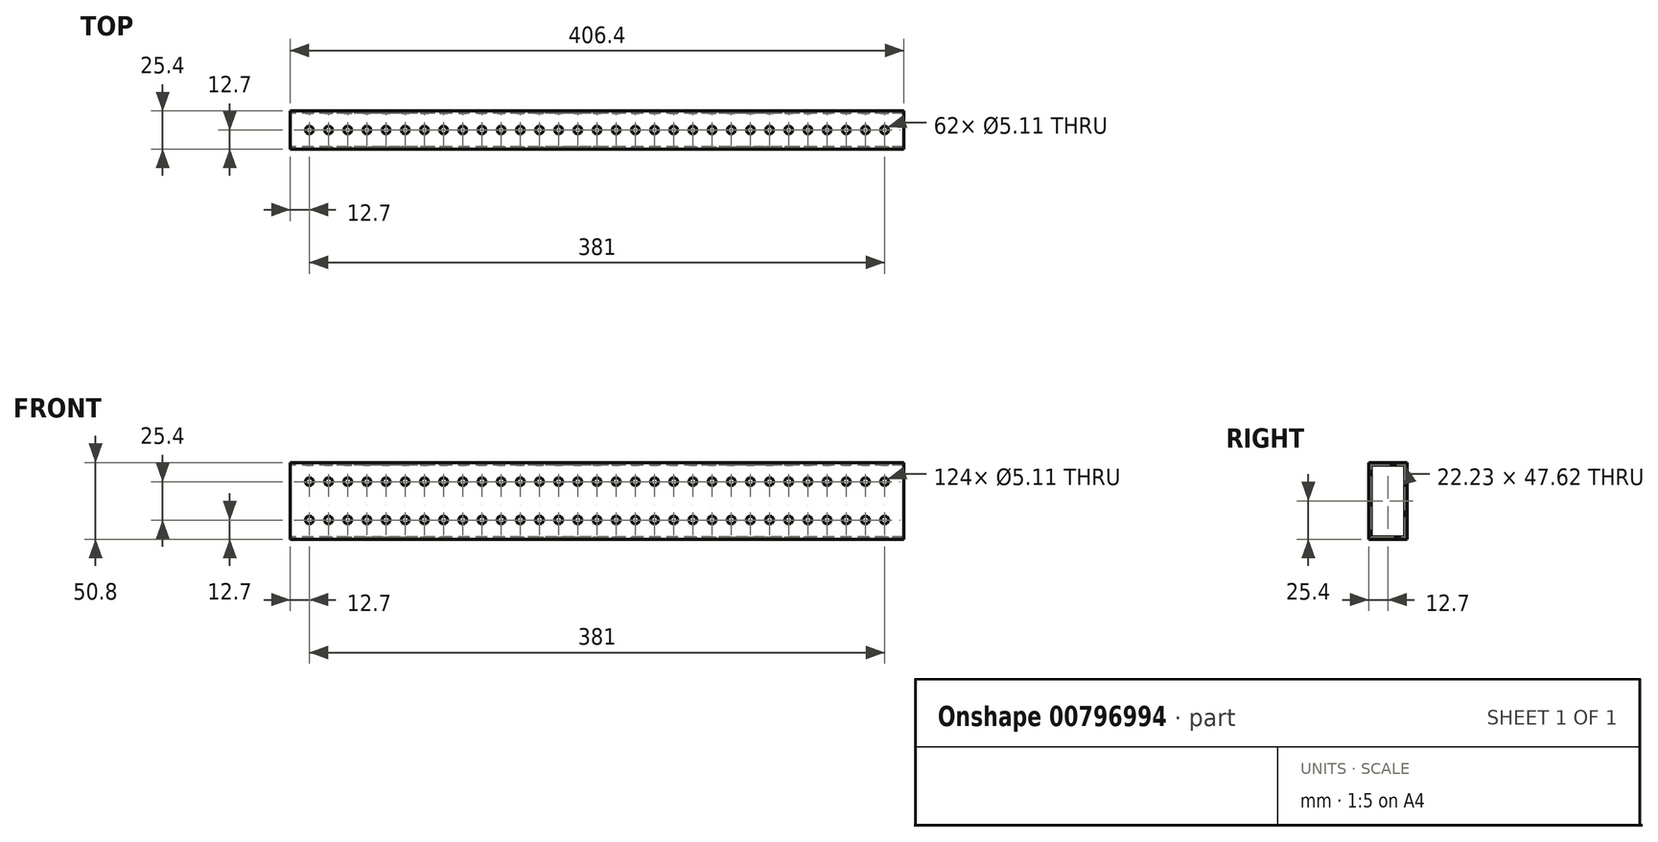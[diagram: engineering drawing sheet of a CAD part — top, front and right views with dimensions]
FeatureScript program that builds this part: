
annotation { "Feature Type Name" : "Feature", "Feature Type Description" : "" }
export const myFeature = defineFeature(function(context is Context, id is Id, definition is map)
    precondition{}
    {
        {
            var Q0;
            Q0=qCreatedBy(makeId("Right.planeOp"),FACE);
            var sketch = newSketch(context, id + "F0", { "sketchPlane" : qUnion([Q0])});
            skLineSegment(sketch, "E0.bottom", {"start": v(12.7, 25.4) * mm, "end": v(-12.7, 25.4) * mm});
            skLineSegment(sketch, "E0.top", {"start": v(12.7, -25.4) * mm, "end": v(-12.7, -25.4) * mm});
            skLineSegment(sketch, "E0.left", {"start": v(12.7, 25.4) * mm, "end": v(12.7, -25.4) * mm});
            skLineSegment(sketch, "E0.right", {"start": v(-12.7, 25.4) * mm, "end": v(-12.7, -25.4) * mm});
            skPoint(sketch, "E0.middle", {"position": v(0, 0) * mm});
            skLineSegment(sketch, "E1.0", {"start": v(-11.11, 23.81) * mm, "end": v(-11.11, -23.81) * mm});
            skLineSegment(sketch, "E1.1", {"start": v(11.11, 23.81) * mm, "end": v(-11.11, 23.81) * mm});
            skLineSegment(sketch, "E1.2", {"start": v(11.11, 23.81) * mm, "end": v(11.11, -23.81) * mm});
            skLineSegment(sketch, "E1.3", {"start": v(11.11, -23.81) * mm, "end": v(-11.11, -23.81) * mm});
            skSolve(sketch);
        }
        {
            var Q0;
            Q0 = qSketchRegion(id + "F0", true);
            extrude(context, id + "F1", {"entities" : qUnion([Q0]), "depth" : 406.4 * mm, "offsetDistance" : 25.4 * mm});
        }
        {
            var Q0;
            Q0=makeQuery(id+"F1.opExtrude","SWEPT_FACE",FACE,{"disambiguationData":[OSD([sQuery(id+"F0.wireOp",EDGE,"E0.bottom")])]});
            var sketch = newSketch(context, id + "F2", { "sketchPlane" : qUnion([Q0])});
            skCircle(sketch, "E2", {"center": v(12.7, 0) * mm, "radius": 2.55 * mm});
            skCircle(sketch, "E3.1.0.0", {"center": v(25.4, 0) * mm, "radius": 2.55 * mm});
            skCircle(sketch, "E3.2.0.0", {"center": v(38.1, 0) * mm, "radius": 2.55 * mm});
            skLineSegment(sketch, "E3.direction1", {"start": v(12.7, 0) * mm, "end": v(25.4, 0) * mm, "construction": true});
            skCircle(sketch, "E4.0.3.0", {"center": v(50.8, 0) * mm, "radius": 2.55 * mm});
            skCircle(sketch, "E4.0.4.0", {"center": v(63.5, 0) * mm, "radius": 2.55 * mm});
            skCircle(sketch, "E4.0.5.0", {"center": v(76.2, 0) * mm, "radius": 2.55 * mm});
            skCircle(sketch, "E4.0.6.0", {"center": v(88.9, 0) * mm, "radius": 2.55 * mm});
            skCircle(sketch, "E4.0.7.0", {"center": v(101.6, 0) * mm, "radius": 2.55 * mm});
            skCircle(sketch, "E4.0.8.0", {"center": v(114.3, 0) * mm, "radius": 2.55 * mm});
            skCircle(sketch, "E4.0.9.0", {"center": v(127, 0) * mm, "radius": 2.55 * mm});
            skCircle(sketch, "E4.0.10.0", {"center": v(139.7, 0) * mm, "radius": 2.55 * mm});
            skCircle(sketch, "E4.0.11.0", {"center": v(152.4, 0) * mm, "radius": 2.55 * mm});
            skCircle(sketch, "E4.0.12.0", {"center": v(165.1, 0) * mm, "radius": 2.55 * mm});
            skCircle(sketch, "E4.0.13.0", {"center": v(177.8, 0) * mm, "radius": 2.55 * mm});
            skCircle(sketch, "E4.0.14.0", {"center": v(190.5, 0) * mm, "radius": 2.55 * mm});
            skCircle(sketch, "E4.0.15.0", {"center": v(203.2, 0) * mm, "radius": 2.55 * mm});
            skCircle(sketch, "E4.0.16.0", {"center": v(215.9, 0) * mm, "radius": 2.55 * mm});
            skCircle(sketch, "E4.0.17.0", {"center": v(228.6, 0) * mm, "radius": 2.55 * mm});
            skCircle(sketch, "E4.0.18.0", {"center": v(241.3, 0) * mm, "radius": 2.55 * mm});
            skCircle(sketch, "E4.0.19.0", {"center": v(254, 0) * mm, "radius": 2.55 * mm});
            skCircle(sketch, "E4.0.20.0", {"center": v(266.7, 0) * mm, "radius": 2.55 * mm});
            skCircle(sketch, "E4.0.21.0", {"center": v(279.4, 0) * mm, "radius": 2.55 * mm});
            skCircle(sketch, "E5.0.22.0", {"center": v(292.1, 0) * mm, "radius": 2.55 * mm});
            skCircle(sketch, "E5.0.23.0", {"center": v(304.8, 0) * mm, "radius": 2.55 * mm});
            skCircle(sketch, "E5.0.24.0", {"center": v(317.5, 0) * mm, "radius": 2.55 * mm});
            skCircle(sketch, "E5.0.25.0", {"center": v(330.2, 0) * mm, "radius": 2.55 * mm});
            skCircle(sketch, "E5.0.26.0", {"center": v(342.9, 0) * mm, "radius": 2.55 * mm});
            skCircle(sketch, "E5.0.27.0", {"center": v(355.6, 0) * mm, "radius": 2.55 * mm});
            skCircle(sketch, "E5.0.28.0", {"center": v(368.3, 0) * mm, "radius": 2.55 * mm});
            skCircle(sketch, "E6.0.29.0", {"center": v(381, 0) * mm, "radius": 2.55 * mm});
            skCircle(sketch, "E7.0.30.0", {"center": v(393.7, 0) * mm, "radius": 2.55 * mm});
            skSolve(sketch);
        }
        {
            var Q0;
            Q0 = qSketchRegion(id + "F2", true);
            extrude(context, id + "F3", {"entities" : qUnion([Q0]), "operationType" : NewBodyOperationType.REMOVE, "endBound" : BoundingType.THROUGH_ALL, "oppositeDirection" : true, "depth" : 254 * mm, "offsetDistance" : 25.4 * mm});
        }
        {
            var Q0;
            Q0=makeQuery(id+"F1.opExtrude","SWEPT_FACE",FACE,{"disambiguationData":[OSD([sQuery(id+"F0.wireOp",EDGE,"E0.right")])]});
            var sketch = newSketch(context, id + "F4", { "sketchPlane" : qUnion([Q0])});
            skCircle(sketch, "E8", {"center": v(12.7, 12.7) * mm, "radius": 2.55 * mm});
            skCircle(sketch, "E9.0.1.0", {"center": v(12.7, -12.7) * mm, "radius": 2.55 * mm});
            skCircle(sketch, "E9.1.0.0", {"center": v(25.4, 12.7) * mm, "radius": 2.55 * mm});
            skCircle(sketch, "E9.1.1.0", {"center": v(25.4, -12.7) * mm, "radius": 2.55 * mm});
            skCircle(sketch, "E9.2.0.0", {"center": v(38.1, 12.7) * mm, "radius": 2.55 * mm});
            skCircle(sketch, "E9.2.1.0", {"center": v(38.1, -12.7) * mm, "radius": 2.55 * mm});
            skCircle(sketch, "E9.3.0.0", {"center": v(50.8, 12.7) * mm, "radius": 2.55 * mm});
            skCircle(sketch, "E9.3.1.0", {"center": v(50.8, -12.7) * mm, "radius": 2.55 * mm});
            skCircle(sketch, "E9.4.0.0", {"center": v(63.5, 12.7) * mm, "radius": 2.55 * mm});
            skCircle(sketch, "E9.4.1.0", {"center": v(63.5, -12.7) * mm, "radius": 2.55 * mm});
            skCircle(sketch, "E9.5.0.0", {"center": v(76.2, 12.7) * mm, "radius": 2.55 * mm});
            skCircle(sketch, "E9.5.1.0", {"center": v(76.2, -12.7) * mm, "radius": 2.55 * mm});
            skCircle(sketch, "E9.6.0.0", {"center": v(88.9, 12.7) * mm, "radius": 2.55 * mm});
            skCircle(sketch, "E9.6.1.0", {"center": v(88.9, -12.7) * mm, "radius": 2.55 * mm});
            skCircle(sketch, "E9.7.0.0", {"center": v(101.6, 12.7) * mm, "radius": 2.55 * mm});
            skCircle(sketch, "E9.7.1.0", {"center": v(101.6, -12.7) * mm, "radius": 2.55 * mm});
            skCircle(sketch, "E9.8.0.0", {"center": v(114.3, 12.7) * mm, "radius": 2.55 * mm});
            skCircle(sketch, "E9.8.1.0", {"center": v(114.3, -12.7) * mm, "radius": 2.55 * mm});
            skCircle(sketch, "E9.9.0.0", {"center": v(127, 12.7) * mm, "radius": 2.55 * mm});
            skCircle(sketch, "E9.9.1.0", {"center": v(127, -12.7) * mm, "radius": 2.55 * mm});
            skCircle(sketch, "E9.10.0.0", {"center": v(139.7, 12.7) * mm, "radius": 2.55 * mm});
            skCircle(sketch, "E9.10.1.0", {"center": v(139.7, -12.7) * mm, "radius": 2.55 * mm});
            skCircle(sketch, "E9.11.0.0", {"center": v(152.4, 12.7) * mm, "radius": 2.55 * mm});
            skCircle(sketch, "E9.11.1.0", {"center": v(152.4, -12.7) * mm, "radius": 2.55 * mm});
            skCircle(sketch, "E9.12.0.0", {"center": v(165.1, 12.7) * mm, "radius": 2.55 * mm});
            skCircle(sketch, "E9.12.1.0", {"center": v(165.1, -12.7) * mm, "radius": 2.55 * mm});
            skCircle(sketch, "E9.13.0.0", {"center": v(177.8, 12.7) * mm, "radius": 2.55 * mm});
            skCircle(sketch, "E9.13.1.0", {"center": v(177.8, -12.7) * mm, "radius": 2.55 * mm});
            skCircle(sketch, "E9.14.0.0", {"center": v(190.5, 12.7) * mm, "radius": 2.55 * mm});
            skCircle(sketch, "E9.14.1.0", {"center": v(190.5, -12.7) * mm, "radius": 2.55 * mm});
            skCircle(sketch, "E9.15.0.0", {"center": v(203.2, 12.7) * mm, "radius": 2.55 * mm});
            skCircle(sketch, "E9.15.1.0", {"center": v(203.2, -12.7) * mm, "radius": 2.55 * mm});
            skCircle(sketch, "E9.16.0.0", {"center": v(215.9, 12.7) * mm, "radius": 2.55 * mm});
            skCircle(sketch, "E9.16.1.0", {"center": v(215.9, -12.7) * mm, "radius": 2.55 * mm});
            skCircle(sketch, "E9.17.0.0", {"center": v(228.6, 12.7) * mm, "radius": 2.55 * mm});
            skCircle(sketch, "E9.17.1.0", {"center": v(228.6, -12.7) * mm, "radius": 2.55 * mm});
            skCircle(sketch, "E9.18.0.0", {"center": v(241.3, 12.7) * mm, "radius": 2.55 * mm});
            skCircle(sketch, "E9.18.1.0", {"center": v(241.3, -12.7) * mm, "radius": 2.55 * mm});
            skCircle(sketch, "E9.19.0.0", {"center": v(254, 12.7) * mm, "radius": 2.55 * mm});
            skCircle(sketch, "E9.19.1.0", {"center": v(254, -12.7) * mm, "radius": 2.55 * mm});
            skCircle(sketch, "E9.20.0.0", {"center": v(266.7, 12.7) * mm, "radius": 2.55 * mm});
            skCircle(sketch, "E9.20.1.0", {"center": v(266.7, -12.7) * mm, "radius": 2.55 * mm});
            skCircle(sketch, "E9.21.0.0", {"center": v(279.4, 12.7) * mm, "radius": 2.55 * mm});
            skCircle(sketch, "E9.21.1.0", {"center": v(279.4, -12.7) * mm, "radius": 2.55 * mm});
            skCircle(sketch, "E9.22.0.0", {"center": v(292.1, 12.7) * mm, "radius": 2.55 * mm});
            skCircle(sketch, "E9.22.1.0", {"center": v(292.1, -12.7) * mm, "radius": 2.55 * mm});
            skCircle(sketch, "E9.23.0.0", {"center": v(304.8, 12.7) * mm, "radius": 2.55 * mm});
            skCircle(sketch, "E9.23.1.0", {"center": v(304.8, -12.7) * mm, "radius": 2.55 * mm});
            skCircle(sketch, "E9.24.0.0", {"center": v(317.5, 12.7) * mm, "radius": 2.55 * mm});
            skCircle(sketch, "E9.24.1.0", {"center": v(317.5, -12.7) * mm, "radius": 2.55 * mm});
            skCircle(sketch, "E9.25.0.0", {"center": v(330.2, 12.7) * mm, "radius": 2.55 * mm});
            skCircle(sketch, "E9.25.1.0", {"center": v(330.2, -12.7) * mm, "radius": 2.55 * mm});
            skCircle(sketch, "E9.26.0.0", {"center": v(342.9, 12.7) * mm, "radius": 2.55 * mm});
            skCircle(sketch, "E9.26.1.0", {"center": v(342.9, -12.7) * mm, "radius": 2.55 * mm});
            skCircle(sketch, "E9.27.0.0", {"center": v(355.6, 12.7) * mm, "radius": 2.55 * mm});
            skCircle(sketch, "E9.27.1.0", {"center": v(355.6, -12.7) * mm, "radius": 2.55 * mm});
            skCircle(sketch, "E9.28.0.0", {"center": v(368.3, 12.7) * mm, "radius": 2.55 * mm});
            skCircle(sketch, "E9.28.1.0", {"center": v(368.3, -12.7) * mm, "radius": 2.55 * mm});
            skCircle(sketch, "E9.29.0.0", {"center": v(381, 12.7) * mm, "radius": 2.55 * mm});
            skCircle(sketch, "E9.29.1.0", {"center": v(381, -12.7) * mm, "radius": 2.55 * mm});
            skCircle(sketch, "E9.30.0.0", {"center": v(393.7, 12.7) * mm, "radius": 2.55 * mm});
            skCircle(sketch, "E9.30.1.0", {"center": v(393.7, -12.7) * mm, "radius": 2.55 * mm});
            skLineSegment(sketch, "E9.direction1", {"start": v(12.7, 12.7) * mm, "end": v(25.4, 12.7) * mm, "construction": true});
            skLineSegment(sketch, "E9.direction2", {"start": v(12.7, 12.7) * mm, "end": v(12.7, -12.7) * mm, "construction": true});
            skSolve(sketch);
        }
        {
            var Q0;
            Q0 = qSketchRegion(id + "F4", true);
            extrude(context, id + "F5", {"entities" : qUnion([Q0]), "operationType" : NewBodyOperationType.REMOVE, "oppositeDirection" : true, "depth" : 76.2 * mm, "offsetDistance" : 25.4 * mm});
        }
    });
